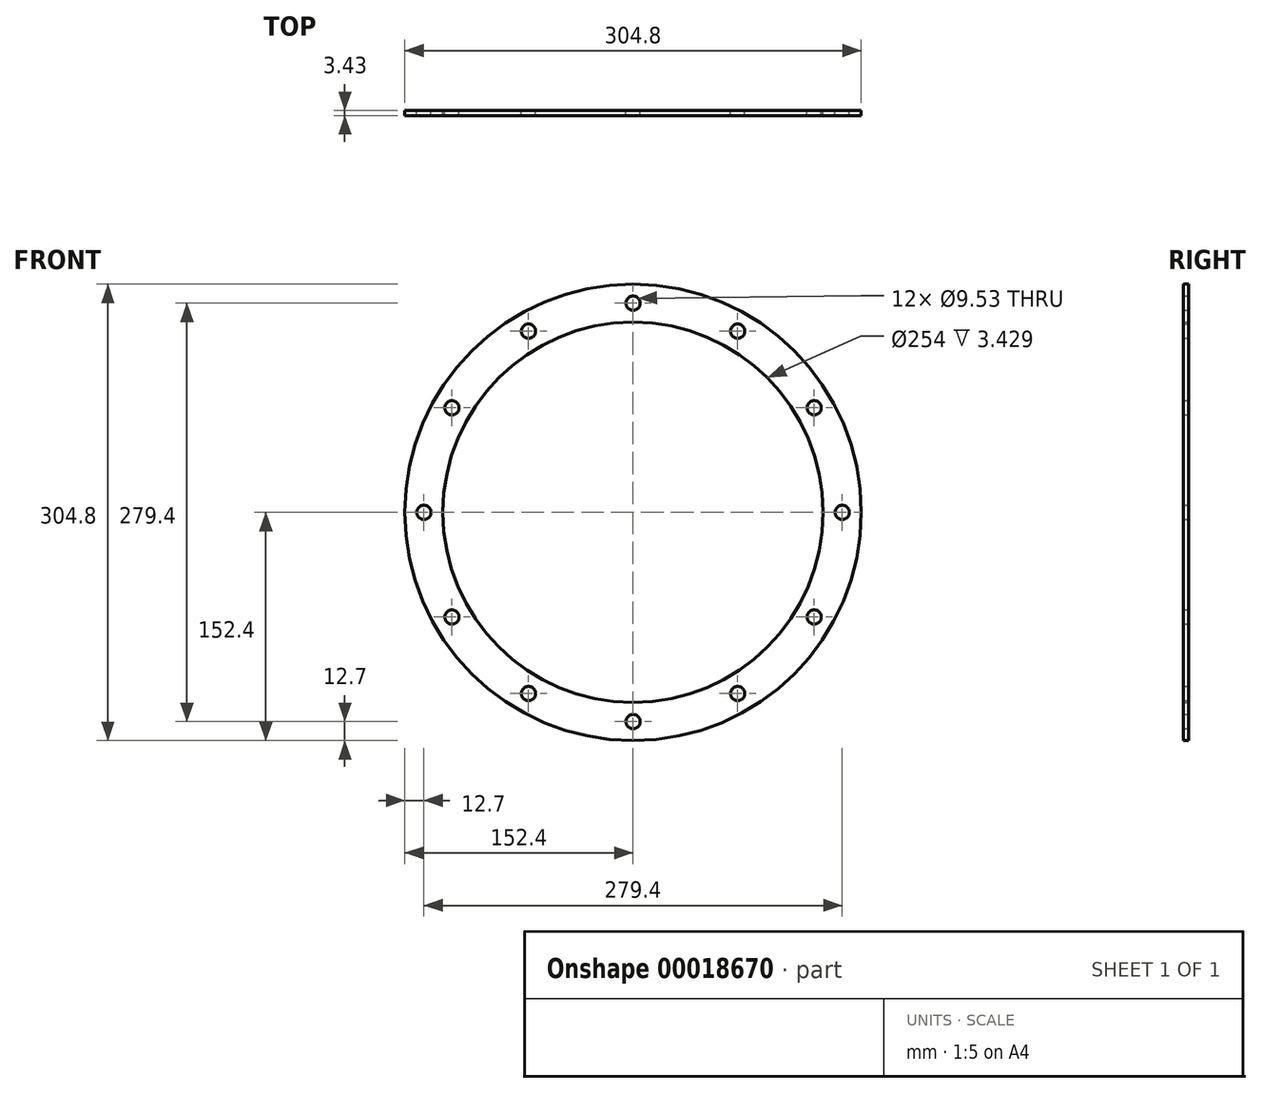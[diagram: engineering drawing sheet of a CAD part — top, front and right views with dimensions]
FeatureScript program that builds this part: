
annotation { "Feature Type Name" : "Feature", "Feature Type Description" : "" }
export const myFeature = defineFeature(function(context is Context, id is Id, definition is map)
    precondition{}
    {
        {
            var Q0;
            Q0=qCreatedBy(makeId("Front.planeOp"),FACE);
            var sketch = newSketch(context, id + "F0", { "sketchPlane" : qUnion([Q0])});
            skCircle(sketch, "E0", {"center": v(0, 0) * mm, "radius": 152.4 * mm});
            skCircle(sketch, "E1", {"center": v(0, 0) * mm, "radius": 127 * mm});
            skCircle(sketch, "E2", {"center": v(0, 139.7) * mm, "radius": 4.76 * mm});
            skCircle(sketch, "E3.1.0", {"center": v(69.85, 120.98) * mm, "radius": 4.76 * mm});
            skCircle(sketch, "E3.2.0", {"center": v(120.98, 69.85) * mm, "radius": 4.76 * mm});
            skCircle(sketch, "E3.3.0", {"center": v(139.7, 0) * mm, "radius": 4.76 * mm});
            skCircle(sketch, "E3.4.0", {"center": v(120.98, -69.85) * mm, "radius": 4.76 * mm});
            skCircle(sketch, "E3.5.0", {"center": v(69.85, -120.98) * mm, "radius": 4.76 * mm});
            skCircle(sketch, "E3.6.0", {"center": v(0, -139.7) * mm, "radius": 4.76 * mm});
            skCircle(sketch, "E3.7.0", {"center": v(-69.85, -120.98) * mm, "radius": 4.76 * mm});
            skCircle(sketch, "E3.8.0", {"center": v(-120.98, -69.85) * mm, "radius": 4.76 * mm});
            skCircle(sketch, "E3.9.0", {"center": v(-139.7, 0) * mm, "radius": 4.76 * mm});
            skCircle(sketch, "E3.10.0", {"center": v(-120.98, 69.85) * mm, "radius": 4.76 * mm});
            skCircle(sketch, "E3.11.0", {"center": v(-69.85, 120.98) * mm, "radius": 4.76 * mm});
            skLineSegment(sketch, "E3.anchor1", {"start": v(0, 0) * mm, "end": v(0, 139.7) * mm, "construction": true});
            skLineSegment(sketch, "E3.anchor2", {"start": v(0, 0) * mm, "end": v(-69.85, 120.98) * mm, "construction": true});
            skSolve(sketch);
        }
        {
            var Q0;
            Q0 = qSketchRegion(id + "F0", true);
            extrude(context, id + "F1", {"entities" : qUnion([Q0]), "depth" : 3.43 * mm});
        }
    });
